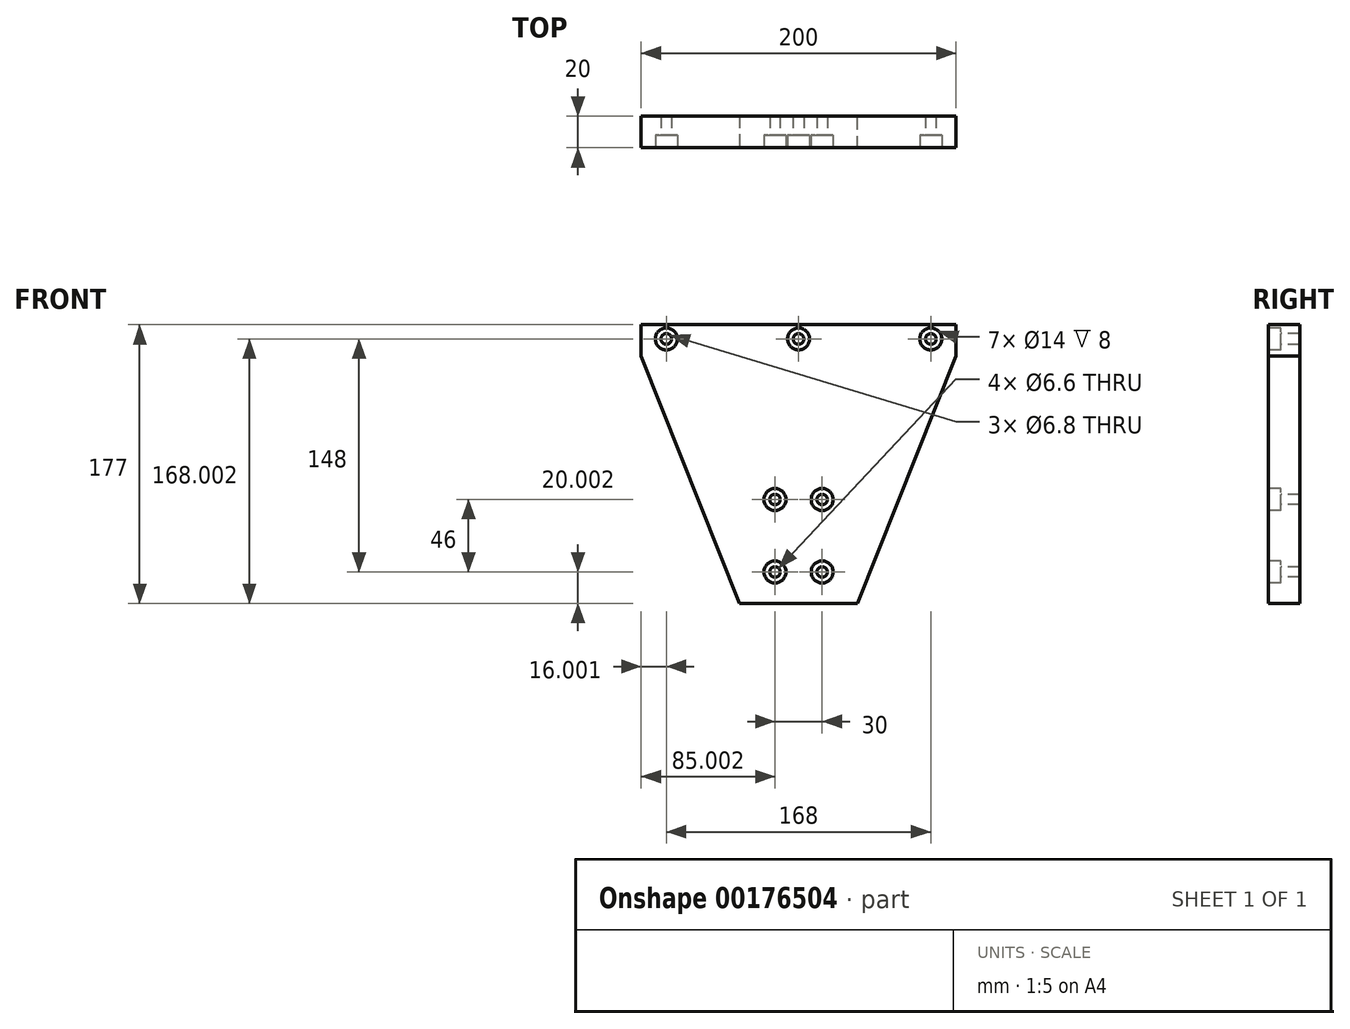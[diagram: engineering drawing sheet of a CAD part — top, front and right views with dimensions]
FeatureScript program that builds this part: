
annotation { "Feature Type Name" : "Feature", "Feature Type Description" : "" }
export const myFeature = defineFeature(function(context is Context, id is Id, definition is map)
    precondition{}
    {
        {
            var Q0;
            Q0=qCreatedBy(makeId("Front.planeOp"),FACE);
            var sketch = newSketch(context, id + "F0", { "sketchPlane" : qUnion([Q0])});
            skLineSegment(sketch, "E0.bottom", {"start": v(-157.56, 149.94) * mm, "end": v(42.44, 149.94) * mm, "construction": true});
            skLineSegment(sketch, "E0.top", {"start": v(-157.56, -26.06) * mm, "end": v(42.44, -26.06) * mm, "construction": true});
            skLineSegment(sketch, "E0.left", {"start": v(-157.56, 149.94) * mm, "end": v(-157.56, -26.06) * mm, "construction": true});
            skLineSegment(sketch, "E0.right", {"start": v(42.44, 149.94) * mm, "end": v(42.44, -26.06) * mm, "construction": true});
            skLineSegment(sketch, "E1", {"start": v(-157.56, 149.94) * mm, "end": v(42.44, 149.94) * mm});
            skLineSegment(sketch, "E2", {"start": v(-57.56, 149.94) * mm, "end": v(-57.56, -26.06) * mm, "construction": true});
            skLineSegment(sketch, "E3", {"start": v(-57.56, -26.06) * mm, "end": v(-87.56, -26.06) * mm});
            skLineSegment(sketch, "E4", {"start": v(-57.56, -26.06) * mm, "end": v(-27.56, -26.06) * mm});
            skLineSegment(sketch, "E5", {"start": v(-87.56, -26.06) * mm, "end": v(-157.56, 149.94) * mm});
            skLineSegment(sketch, "E6", {"start": v(-27.56, -26.06) * mm, "end": v(42.44, 149.94) * mm});
            skSolve(sketch);
        }
        {
            var Q0;
            Q0=makeQuery(id+"F0.imprint","IMPRINT",FACE,{"disambiguationData":[TD([[makeQuery(id+"F0.imprint","IMPRINT",EDGE,{"derivedFrom":sQuery(id+"F0.wireOp",EDGE,"E1")}),-1.0]])]});
            extrude(context, id + "F1", {"entities" : qUnion([Q0]), "depth" : 20.5 * mm});
        }
        {
            var Q0;
            Q0=makeQuery(id+"F1.opExtrude","CAP_FACE",FACE,{"disambiguationData":[OSD([sQuery(id+"F0.wireOp",EDGE,"E1"),sQuery(id+"F0.wireOp",EDGE,"E3"),sQuery(id+"F0.wireOp",EDGE,"E4"),sQuery(id+"F0.wireOp",EDGE,"E5"),sQuery(id+"F0.wireOp",EDGE,"E6")])],"isStart":false});
            var sketch = newSketch(context, id + "F2", { "sketchPlane" : qUnion([Q0])});
            skLineSegment(sketch, "E7.bottom", {"start": v(-157.56, 149.94) * mm, "end": v(42.44, 149.94) * mm});
            skLineSegment(sketch, "E7.top", {"start": v(-157.56, 169.94) * mm, "end": v(42.44, 169.94) * mm});
            skLineSegment(sketch, "E7.left", {"start": v(-157.56, 149.94) * mm, "end": v(-157.56, 169.94) * mm});
            skLineSegment(sketch, "E7.right", {"start": v(42.44, 149.94) * mm, "end": v(42.44, 169.94) * mm});
            skSolve(sketch);
        }
        {
            var Q0;
            Q0=makeQuery(id+"F2.imprint","IMPRINT",FACE,{"disambiguationData":[TD([[makeQuery(id+"F2.imprint","IMPRINT",EDGE,{"derivedFrom":sQuery(id+"F2.wireOp",EDGE,"E7.bottom")}),1.0]])]});
            extrude(context, id + "F3", {"entities" : qUnion([Q0]), "operationType" : NewBodyOperationType.ADD, "oppositeDirection" : true, "depth" : 20.5 * mm});
        }
        {
            var Q0;
            Q0=makeQuery(id+"F1.opExtrude","SWEPT_FACE",FACE,{"disambiguationData":[OSD([sQuery(id+"F0.wireOp",EDGE,"E3"),sQuery(id+"F0.wireOp",EDGE,"E4")])]});
            extrude(context, id + "F4", {"entities" : qUnion([Q0]), "operationType" : NewBodyOperationType.REMOVE, "oppositeDirection" : true, "depth" : 19 * mm});
        }
        {
            var Q0;
            Q0=makeQuery(id+"F4.boolean.opBoolean","COPY",FACE,{"derivedFrom":makeQuery(id+"F4.opExtrude","SWEPT_FACE",FACE,{"disambiguationData":[OSD([sQuery(id+"F0.wireOp",EDGE,"E3"),sQuery(id+"F0.wireOp",EDGE,"E5")])]})});
            extrude(context, id + "F5", {"entities" : qUnion([Q0]), "operationType" : NewBodyOperationType.REMOVE, "oppositeDirection" : true, "depth" : 25 * mm});
        }
        {
            var Q0;
            Q0=makeQuery(id+"F4.boolean.opBoolean","COPY",FACE,{"derivedFrom":makeQuery(id+"F4.opExtrude","SWEPT_FACE",FACE,{"disambiguationData":[OSD([sQuery(id+"F0.wireOp",EDGE,"E4"),sQuery(id+"F0.wireOp",EDGE,"E6")])]})});
            extrude(context, id + "F6", {"entities" : qUnion([Q0]), "operationType" : NewBodyOperationType.REMOVE, "oppositeDirection" : true, "depth" : 25 * mm});
        }
        {
            var Q0;
            Q0=makeQuery(id+"F3.boolean.opBoolean","MERGE",FACE,{"derivedFrom":[makeQuery(id+"F1.opExtrude","CAP_FACE",FACE,{"disambiguationData":[OSD([sQuery(id+"F0.wireOp",EDGE,"E1"),sQuery(id+"F0.wireOp",EDGE,"E3"),sQuery(id+"F0.wireOp",EDGE,"E4"),sQuery(id+"F0.wireOp",EDGE,"E5"),sQuery(id+"F0.wireOp",EDGE,"E6")])],"isStart":false}),makeQuery(id+"F3.opExtrude","CAP_FACE",FACE,{"disambiguationData":[OSD([sQuery(id+"F2.wireOp",EDGE,"E7.bottom"),sQuery(id+"F2.wireOp",EDGE,"E7.top"),sQuery(id+"F2.wireOp",EDGE,"E7.left"),sQuery(id+"F2.wireOp",EDGE,"E7.right")])],"isStart":true})]});
            var sketch = newSketch(context, id + "F7", { "sketchPlane" : qUnion([Q0])});
            skLineSegment(sketch, "E8", {"start": v(-217.07, 5.94) * mm, "end": v(104.37, 5.94) * mm, "construction": true});
            skLineSegment(sketch, "E9", {"start": v(-84.66, -7.06) * mm, "end": v(24.62, -7.06) * mm, "construction": true});
            skSolve(sketch);
        }
        {
            var Q0;
            Q0=makeQuery(id+"F7.imprint","IMPRINT",FACE,{"disambiguationData":[TD([[makeQuery(id+"F7.imprint","IMPRINT",EDGE,{"derivedFrom":makeQuery(id+"F3.opExtrude","CAP_EDGE",EDGE,{"disambiguationData":[OSD([sQuery(id+"F2.wireOp",EDGE,"E7.top")])],"isStart":true})}),-1.0]])]});
            var sketch = newSketch(context, id + "F8", { "sketchPlane" : qUnion([Q0])});
            skPoint(sketch, "E10", {"position": v(-72.56, 12.94) * mm});
            skPoint(sketch, "E11", {"position": v(-42.56, 12.94) * mm});
            skPoint(sketch, "E12", {"position": v(-42.56, 58.94) * mm});
            skPoint(sketch, "E13", {"position": v(-72.56, 58.94) * mm});
            skSolve(sketch);
        }
        {
            var Q0;
            Q0=sQuery(id+"F8.wireOp",VERTEX,"E13");
            var Q1;
            Q1=sQuery(id+"F8.wireOp",VERTEX,"E12");
            var Q2;
            Q2=sQuery(id+"F8.wireOp",VERTEX,"E11");
            var Q3;
            Q3=sQuery(id+"F8.wireOp",VERTEX,"E10");
            var Q4;
            Q4=makeQuery(id+"F1.opExtrude","SWEPT_BODY",BODY,{"disambiguationData":[OSD([sQuery(id+"F0.wireOp",EDGE,"E1"),sQuery(id+"F0.wireOp",EDGE,"E3"),sQuery(id+"F0.wireOp",EDGE,"E4"),sQuery(id+"F0.wireOp",EDGE,"E5"),sQuery(id+"F0.wireOp",EDGE,"E6")])]});
            hole(context, id + "F9", {"style" : HoleStyle.C_BORE, "endStyle" : HoleEndStyle.THROUGH, "standardTappedOrClearance" : lookupTablePath({ "standard" : "ISO", "engagement" : "75%", "pitch" : "1.25 mm", "size" : "M8", "type" : "Tapped" }), "standardBlindInLast" : lookupTablePath({ "standard" : "ISO", "engagement" : "75%", "pitch" : "1.25 mm", "size" : "M8", "type" : "Tapped" }), "holeDiameter" : 6.6 * mm, "cBoreDiameter" : 14 * mm, "cBoreDepth" : 8 * mm, "locations" : qUnion([Q0, Q1, Q2, Q3]), "scope" : qUnion([Q4]), "isTappedThrough" : true, "majorDiameter" : 8 * mm, "showTappedDepth" : true});
        }
        {
            var Q0;
            Q0=makeQuery(id+"F7.imprint","IMPRINT",FACE,{"disambiguationData":[TD([[makeQuery(id+"F7.imprint","IMPRINT",EDGE,{"derivedFrom":makeQuery(id+"F3.opExtrude","CAP_EDGE",EDGE,{"disambiguationData":[OSD([sQuery(id+"F2.wireOp",EDGE,"E7.top")])],"isStart":true})}),-1.0]])]});
            var sketch = newSketch(context, id + "F10", { "sketchPlane" : qUnion([Q0])});
            skPoint(sketch, "E14", {"position": v(-141.56, 160.94) * mm});
            skPoint(sketch, "E15", {"position": v(26.44, 160.94) * mm});
            skLineSegment(sketch, "E16", {"start": v(-141.56, 160.94) * mm, "end": v(26.44, 160.94) * mm, "construction": true});
            skPoint(sketch, "E17", {"position": v(-57.56, 160.94) * mm});
            skSolve(sketch);
        }
        {
            var Q0;
            Q0=sQuery(id+"F10.wireOp",VERTEX,"E14");
            var Q1;
            Q1=sQuery(id+"F10.wireOp",VERTEX,"E15");
            var Q2;
            Q2=sQuery(id+"F10.wireOp",VERTEX,"E17");
            var Q3;
            Q3=makeQuery(id+"F1.opExtrude","SWEPT_BODY",BODY,{"disambiguationData":[OSD([sQuery(id+"F0.wireOp",EDGE,"E1"),sQuery(id+"F0.wireOp",EDGE,"E3"),sQuery(id+"F0.wireOp",EDGE,"E4"),sQuery(id+"F0.wireOp",EDGE,"E5"),sQuery(id+"F0.wireOp",EDGE,"E6")])]});
            hole(context, id + "F11", {"style" : HoleStyle.C_BORE, "endStyle" : HoleEndStyle.THROUGH, "holeDiameter" : 6.8 * mm, "cBoreDiameter" : 14 * mm, "cBoreDepth" : 8 * mm, "locations" : qUnion([Q0, Q1, Q2]), "scope" : qUnion([Q3]), "isTappedThrough" : true});
        }
        {
            var Q0;
            Q0=makeQuery(id+"F3.boolean.opBoolean","MERGE",FACE,{"derivedFrom":[makeQuery(id+"F1.opExtrude","CAP_FACE",FACE,{"disambiguationData":[OSD([sQuery(id+"F0.wireOp",EDGE,"E1"),sQuery(id+"F0.wireOp",EDGE,"E3"),sQuery(id+"F0.wireOp",EDGE,"E4"),sQuery(id+"F0.wireOp",EDGE,"E5"),sQuery(id+"F0.wireOp",EDGE,"E6")])],"isStart":true}),makeQuery(id+"F3.opExtrude","CAP_FACE",FACE,{"disambiguationData":[OSD([sQuery(id+"F2.wireOp",EDGE,"E7.bottom"),sQuery(id+"F2.wireOp",EDGE,"E7.top"),sQuery(id+"F2.wireOp",EDGE,"E7.left"),sQuery(id+"F2.wireOp",EDGE,"E7.right")])],"isStart":false})]});
            extrude(context, id + "F12", {"entities" : qUnion([Q0]), "operationType" : NewBodyOperationType.REMOVE, "oppositeDirection" : true, "depth" : .5 * mm});
        }
    });
